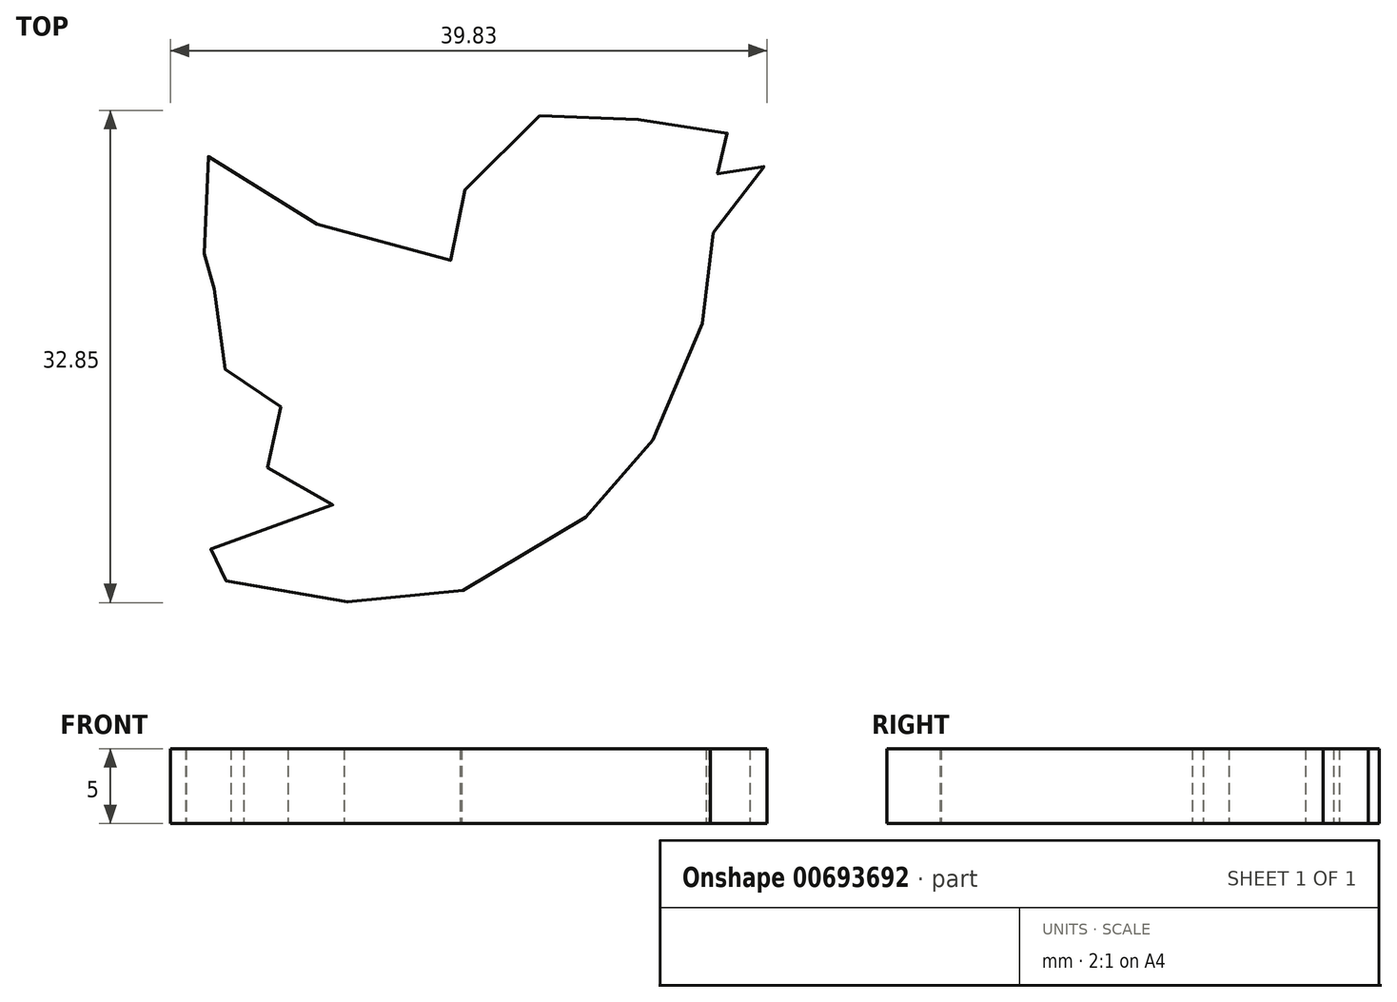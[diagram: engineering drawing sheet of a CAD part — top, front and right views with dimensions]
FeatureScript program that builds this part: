
annotation { "Feature Type Name" : "Feature", "Feature Type Description" : "" }
export const myFeature = defineFeature(function(context is Context, id is Id, definition is map)
    precondition{}
    {
        {
            var Q0;
            Q0=qCreatedBy(makeId("Top.planeOp"),FACE);
            var sketch = newSketch(context, id + "F0", { "sketchPlane" : qUnion([Q0])});
            skFitSpline(sketch, "E0", {"points": [v(-56.77, -1.08) * mm, v(-56.95, -3.84) * mm, v(-57.33, -6.6) * mm, v(-59.52, -12.72) * mm, v(-61.4, -15.76) * mm, v(-63.4, -18.19) * mm, v(-67.56, -21.93) * mm, v(-74.3, -25.2) * mm, v(-79.48, -25.76) * mm, v(-82.52, -25.67) * mm, v(-87.98, -24.78) * mm, v(-92.99, -22.26) * mm, v(-90.42, -22.2) * mm, v(-83.83, -20.2) * mm, v(-81.54, -18.84) * mm, v(-81.4, -18.7) * mm, v(-84.76, -17.82) * mm, v(-88.87, -13.33) * mm, v(-85.46, -12.68) * mm, v(-85.13, -12.58) * mm, v(-87.24, -12.02) * mm, v(-90.27, -8.75) * mm, v(-91.68, -4.73) * mm, v(-88.13, -5.38) * mm, v(-88.97, -4.68) * mm, v(-91.3, -1.13) * mm, v(-91.54, 3.78) * mm, v(-88.27, 3.07) * mm, v(-83.22, -0.48) * mm, v(-75.5, -2.58) * mm, v(-73.78, -2.9) * mm, v(-73.54, -2.07) * mm, v(-73.45, 1.44) * mm, v(-71.25, 4.34) * mm, v(-68.12, 6.81) * mm, v(-64.66, 7) * mm, v(-61.44, 6.3) * mm, v(-59.29, 4.48) * mm, v(-55.08, 6.02) * mm, v(-54.34, 6.3) * mm, v(-55.74, 3.5) * mm, v(-57.23, 2.23) * mm, v(-55.41, 2.56) * mm, v(-53.21, 3.3) * mm, v(-54.1, 1.49) * mm, v(-56.77, -1.08) * mm]});
            skSolve(sketch);
        }
        {
            var Q0;
            Q0 = qSketchRegion(id + "F0", true);
            extrude(context, id + "F1", {"entities" : qUnion([Q0]), "depth" : 5 * mm, "offsetDistance" : 25.4 * mm});
        }
    });
